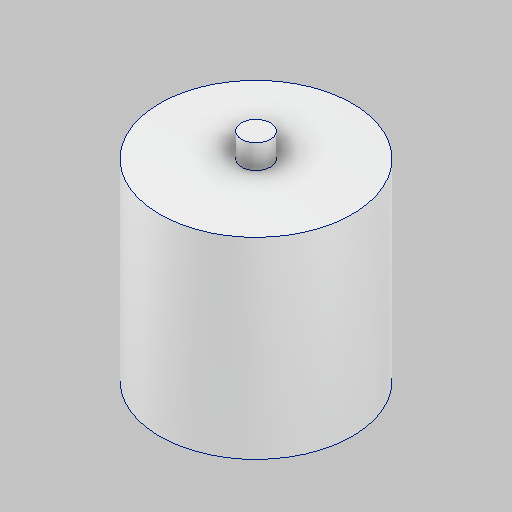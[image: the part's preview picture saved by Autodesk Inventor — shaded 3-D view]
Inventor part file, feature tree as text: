
AUTODESK INVENTOR PART (.ipt)
format: ipt  version: 2025.2 (Build 292293000, 293)  size: 212,480 bytes
history: native  units: in
note: dims shown in document units (in); Inventor stores cm internally (conversion verified against a paired STEP export)
features: extrude x2, sketch x2
ambient origin geometry x8: Origin, YZ Plane, XZ Plane, XY Plane, X Axis, Y Axis, Z Axis, Center Point
bodies: Solid1 (feature_tree)
feature tree (4):
  extrude  "Extrusion1"  Depth=1.5748in TaperAngle=0.0deg
  extrude  "Extrusion2"  Depth=0.1969in TaperAngle=0.0deg
  sketch  "Sketch1"  dims[d0=1.5748in d1=1.5748in d2=0.0in]
  sketch  "Sketch2"  dims[d3=0.2362in d4=0.1969in d5=0.0in]
